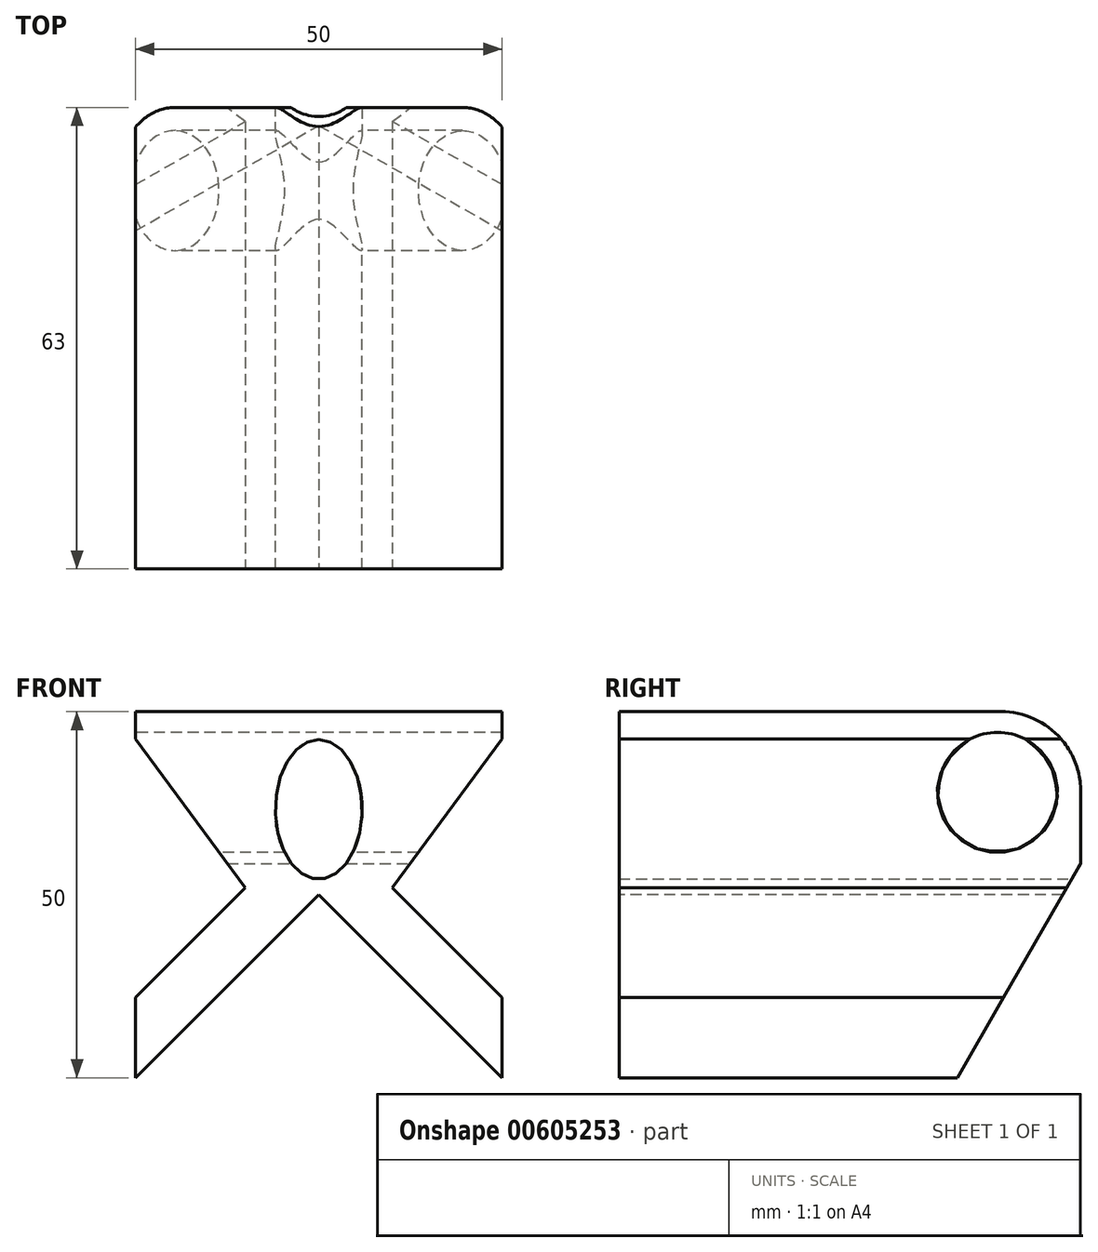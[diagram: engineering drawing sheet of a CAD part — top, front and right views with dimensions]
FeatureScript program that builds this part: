
annotation { "Feature Type Name" : "Feature", "Feature Type Description" : "" }
export const myFeature = defineFeature(function(context is Context, id is Id, definition is map)
    precondition{}
    {
        {
            var Q0;
            Q0=qCreatedBy(makeId("Top.planeOp"),FACE);
            var sketch = newSketch(context, id + "F0", { "sketchPlane" : qUnion([Q0])});
            skLineSegment(sketch, "E0.bottom", {"start": v(25, -45) * mm, "end": v(-25, -45) * mm});
            skLineSegment(sketch, "E0.top", {"start": v(25, 45) * mm, "end": v(-25, 45) * mm});
            skLineSegment(sketch, "E0.left", {"start": v(25, -45) * mm, "end": v(25, 45) * mm});
            skLineSegment(sketch, "E0.right", {"start": v(-25, -45) * mm, "end": v(-25, 45) * mm});
            skPoint(sketch, "E0.middle", {"position": v(0, 0) * mm});
            skSolve(sketch);
        }
        {
            var Q0;
            Q0=makeQuery(id+"F0.imprint","IMPRINT",FACE,{"disambiguationData":[TD([[makeQuery(id+"F0.imprint","IMPRINT",EDGE,{"derivedFrom":sQuery(id+"F0.wireOp",EDGE,"E0.bottom")}),-1.0]])]});
            extrude(context, id + "F1", {"entities" : qUnion([Q0]), "depth" : 50 * mm, "offsetDistance" : 25 * mm});
        }
        {
            var Q0;
            Q0=makeQuery(id+"F1.opExtrude","SWEPT_FACE",FACE,{"disambiguationData":[OSD([sQuery(id+"F0.wireOp",EDGE,"E0.bottom")])]});
            var sketch = newSketch(context, id + "F2", { "sketchPlane" : qUnion([Q0])});
            skLineSegment(sketch, "E1", {"start": v(-25, 0) * mm, "end": v(25, 0) * mm});
            skLineSegment(sketch, "E2", {"start": v(25, 0) * mm, "end": v(0, 25) * mm});
            skLineSegment(sketch, "E3", {"start": v(0, 25) * mm, "end": v(-25, 0) * mm});
            skSolve(sketch);
        }
        {
            var Q0;
            Q0=makeQuery(id+"F2.imprint","IMPRINT",FACE,{"disambiguationData":[TD([[makeQuery(id+"F2.imprint","IMPRINT",EDGE,{"derivedFrom":sQuery(id+"F2.wireOp",EDGE,"E1")}),-1.0]])]});
            extrude(context, id + "F3", {"entities" : qUnion([Q0]), "operationType" : NewBodyOperationType.REMOVE, "endBound" : BoundingType.THROUGH_ALL, "oppositeDirection" : true, "depth" : 25 * mm, "offsetDistance" : 25 * mm});
        }
        {
            var Q0;
            Q0=makeQuery(id+"F1.opExtrude","SWEPT_FACE",FACE,{"disambiguationData":[OSD([sQuery(id+"F0.wireOp",EDGE,"E0.right")])]});
            var sketch = newSketch(context, id + "F4", { "sketchPlane" : qUnion([Q0])});
            skCircle(sketch, "E4", {"center": v(-33.66, 38.97) * mm, "radius": 8.2 * mm});
            skSolve(sketch);
        }
        {
            var Q0;
            Q0=makeQuery(id+"F4.imprint","IMPRINT",FACE,{"disambiguationData":[TD([[makeQuery(id+"F4.imprint","IMPRINT",EDGE,{"derivedFrom":sQuery(id+"F4.wireOp",EDGE,"E4")}),1.0]])]});
            extrude(context, id + "F5", {"entities" : qUnion([Q0]), "operationType" : NewBodyOperationType.REMOVE, "endBound" : BoundingType.THROUGH_ALL, "oppositeDirection" : true, "depth" : 25 * mm, "offsetDistance" : 25 * mm});
        }
        {
            var Q0;
            Q0=makeQuery(id+"F1.opExtrude","CAP_EDGE",EDGE,{"disambiguationData":[OSD([sQuery(id+"F0.wireOp",EDGE,"E0.top")])],"isStart":false});
            fillet(context, id + "F6", {"entities" : qUnion([Q0]), "radius" : 10.86 * mm, "tangentPropagation" : true, "allowEdgeOverflow" : false});
        }
        {
            var Q0;
            Q0=makeQuery(id+"F1.opExtrude","SWEPT_FACE",FACE,{"disambiguationData":[OSD([sQuery(id+"F0.wireOp",EDGE,"E0.left")])]});
            var sketch = newSketch(context, id + "F7", { "sketchPlane" : qUnion([Q0])});
            skLineSegment(sketch, "E5", {"start": v(45, 0) * mm, "end": v(45, 29.26) * mm});
            skLineSegment(sketch, "E6", {"start": v(45, 29.26) * mm, "end": v(28.2, 0) * mm});
            skLineSegment(sketch, "E7", {"start": v(28.2, 0) * mm, "end": v(45, 0) * mm});
            skSolve(sketch);
        }
        {
            var Q0;
            Q0=makeQuery(id+"F7.imprint","IMPRINT",FACE,{"disambiguationData":[TD([[makeQuery(id+"F7.imprint","IMPRINT",EDGE,{"derivedFrom":sQuery(id+"F7.wireOp",EDGE,"E5")}),-1.0]])]});
            extrude(context, id + "F8", {"entities" : qUnion([Q0]), "operationType" : NewBodyOperationType.REMOVE, "endBound" : BoundingType.THROUGH_ALL, "oppositeDirection" : true, "depth" : 25 * mm, "offsetDistance" : 25 * mm});
        }
        {
            var Q0;
            Q0=makeQuery(id+"F1.opExtrude","SWEPT_FACE",FACE,{"disambiguationData":[OSD([sQuery(id+"F0.wireOp",EDGE,"E0.bottom")])]});
            var sketch = newSketch(context, id + "F9", { "sketchPlane" : qUnion([Q0])});
            skLineSegment(sketch, "E8", {"start": v(-25, 10.97) * mm, "end": v(-10.04, 25.93) * mm});
            skLineSegment(sketch, "E9", {"start": v(-10.04, 25.93) * mm, "end": v(-25, 46.25) * mm});
            skLineSegment(sketch, "E10", {"start": v(-25, 46.25) * mm, "end": v(-25, 10.97) * mm});
            skLineSegment(sketch, "E11", {"start": v(0, 25) * mm, "end": v(0, 45.6) * mm, "construction": true});
            skLineSegment(sketch, "E12.MirrorCS", {"start": v(10.04, 25.93) * mm, "end": v(25, 46.25) * mm});
            skLineSegment(sketch, "E13.MirrorCS", {"start": v(25, 10.97) * mm, "end": v(10.04, 25.93) * mm});
            skLineSegment(sketch, "E14.MirrorCS", {"start": v(25, 46.25) * mm, "end": v(25, 10.97) * mm});
            skSolve(sketch);
        }
        {
            var Q0;
            Q0=makeQuery(id+"F1.opExtrude","SWEPT_FACE",FACE,{"disambiguationData":[OSD([sQuery(id+"F0.wireOp",EDGE,"E0.bottom")])]});
            var sketch = newSketch(context, id + "F10", { "sketchPlane" : qUnion([Q0])});
            skEllipse(sketch, "E15", {"center": v(0, 36.65) * mm, "majorRadius": 9.52 * mm, "minorRadius": 5.92 * mm, "majorAxis": v(0, 1)});
            skSolve(sketch);
        }
        {
            var Q0;
            Q0=makeQuery(id+"F10.imprint","IMPRINT",FACE,{"disambiguationData":[TD([[makeQuery(id+"F10.imprint","IMPRINT",EDGE,{"derivedFrom":sQuery(id+"F10.wireOp",EDGE,"E15")}),1.0]])]});
            extrude(context, id + "F11", {"entities" : qUnion([Q0]), "operationType" : NewBodyOperationType.REMOVE, "endBound" : BoundingType.THROUGH_ALL, "oppositeDirection" : true, "depth" : 25 * mm, "offsetDistance" : 25 * mm});
        }
        {
            var Q0;
            Q0=makeQuery(id+"F1.opExtrude","SWEPT_FACE",FACE,{"disambiguationData":[OSD([sQuery(id+"F0.wireOp",EDGE,"E0.bottom")])]});
            var sketch = newSketch(context, id + "F12", { "sketchPlane" : qUnion([Q0])});
            skLineSegment(sketch, "E16.bottom", {"start": v(-34.71, 7.27) * mm, "end": v(34.71, 7.27) * mm});
            skLineSegment(sketch, "E16.top", {"start": v(-34.71, -7.27) * mm, "end": v(34.71, -7.27) * mm});
            skLineSegment(sketch, "E16.left", {"start": v(-34.71, 7.27) * mm, "end": v(-34.71, -7.27) * mm});
            skLineSegment(sketch, "E16.right", {"start": v(34.71, 7.27) * mm, "end": v(34.71, -7.27) * mm});
            skPoint(sketch, "E16.middle", {"position": v(0, 0) * mm});
            skSolve(sketch);
        }
        {
            var Q0;
            {var subQ0=sQuery(id+"F12.wireOp",EDGE,"E16.bottom");var subQ3=sQuery(id+"F2.wireOp",EDGE,"E2");var subQ6=makeQuery(id+"F3.boolean.opBoolean","COPY",EDGE,{"derivedFrom":makeQuery(id+"F3.opExtrude","CAP_EDGE",EDGE,{"disambiguationData":[OSD([subQ3])],"isStart":true})});var subQ7=makeQuery(id+"F12.imprint","INTERSECT",VERTEX,{"derivedFrom":[subQ6,subQ0]});Q0=makeQuery(id+"F12.imprint","IMPRINT",FACE,{"disambiguationData":[TD([[makeQuery(id+"F12.imprint","IMPRINT",EDGE,{"disambiguationData":[TD([[subQ7,-1.0]])],"derivedFrom":subQ0}),-1.0]])]});}
            var Q1;
            {var subQ0=sQuery(id+"F12.wireOp",EDGE,"E16.bottom");var subQ3=sQuery(id+"F2.wireOp",EDGE,"E3");var subQ6=makeQuery(id+"F3.boolean.opBoolean","COPY",EDGE,{"derivedFrom":makeQuery(id+"F3.opExtrude","CAP_EDGE",EDGE,{"disambiguationData":[OSD([subQ3])],"isStart":true})});var subQ7=makeQuery(id+"F12.imprint","INTERSECT",VERTEX,{"derivedFrom":[subQ6,subQ0]});Q1=makeQuery(id+"F12.imprint","IMPRINT",FACE,{"disambiguationData":[TD([[makeQuery(id+"F12.imprint","IMPRINT",EDGE,{"disambiguationData":[TD([[subQ7,1.0]])],"derivedFrom":subQ0}),-1.0]])]});}
            extrude(context, id + "F13", {"entities" : qUnion([Q0, Q1]), "operationType" : NewBodyOperationType.REMOVE, "endBound" : BoundingType.THROUGH_ALL, "oppositeDirection" : true, "depth" : 25 * mm, "offsetDistance" : 25 * mm});
        }
        {
            var Q0;
            Q0=makeQuery(id+"F9.imprint","IMPRINT",FACE,{"disambiguationData":[TD([[makeQuery(id+"F9.imprint","IMPRINT",EDGE,{"derivedFrom":sQuery(id+"F9.wireOp",EDGE,"E12.MirrorCS")}),-1.0]])]});
            var Q1;
            Q1=makeQuery(id+"F9.imprint","IMPRINT",FACE,{"disambiguationData":[TD([[makeQuery(id+"F9.imprint","IMPRINT",EDGE,{"derivedFrom":sQuery(id+"F9.wireOp",EDGE,"E8")}),1.0]])]});
            extrude(context, id + "F14", {"entities" : qUnion([Q0, Q1]), "operationType" : NewBodyOperationType.REMOVE, "endBound" : BoundingType.THROUGH_ALL, "oppositeDirection" : true, "depth" : 25 * mm, "offsetDistance" : 25 * mm});
        }
        {
            var Q0;
            Q0=makeQuery(id+"F1.opExtrude","SWEPT_FACE",FACE,{"disambiguationData":[OSD([sQuery(id+"F0.wireOp",EDGE,"E0.bottom")])]});
            extrude(context, id + "F15", {"entities" : qUnion([Q0]), "operationType" : NewBodyOperationType.REMOVE, "oppositeDirection" : true, "depth" : 27 * mm, "offsetDistance" : 25 * mm});
        }
    });
